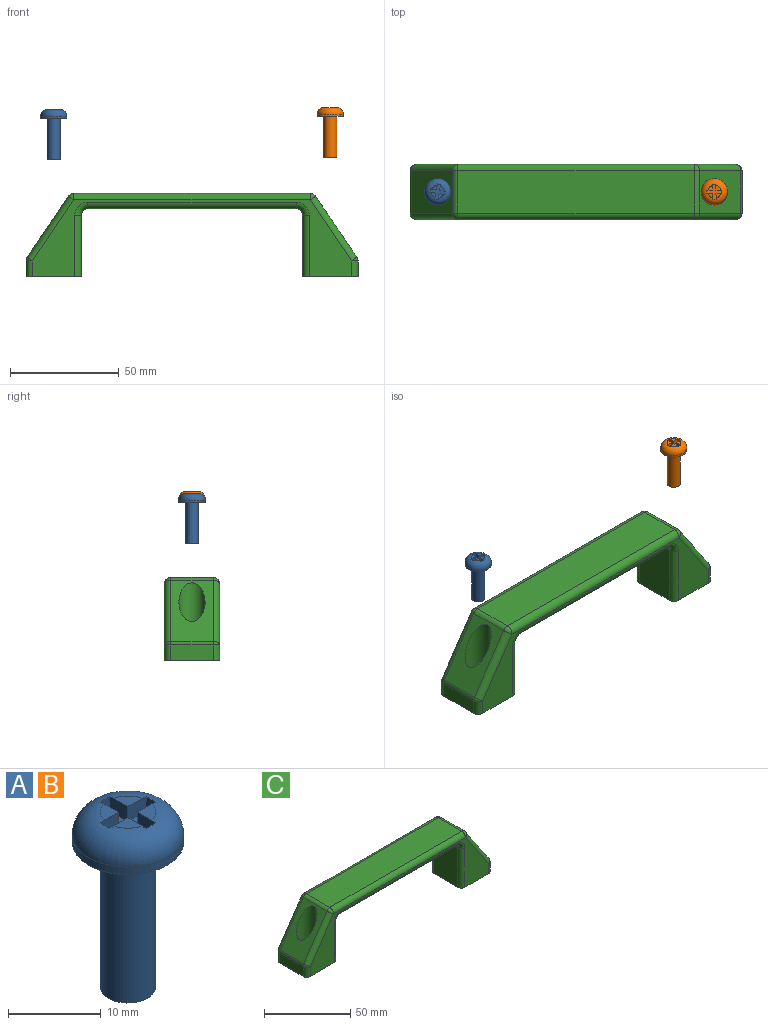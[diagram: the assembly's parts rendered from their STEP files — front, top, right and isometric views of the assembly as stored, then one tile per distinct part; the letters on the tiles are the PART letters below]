
ASSEMBLY  parts=3 mates=2
PART A: 22 faces, bbox 13x13x23.1 mm
  f0: plane 2.15x2.15mm, normal (0,0,1), area 3.2mm2, adj f3,f12,f13
  f1: plane 2.15x2.15mm, normal (0,0,1), area 3.2mm2, adj f3,f15,f16
  f2: plane 2.15x2.15mm, normal (0,0,1), area 3.2mm2, adj f3,f7,f18
  f3: torus R=3mm, axis (0,0,1), area 142.1mm2, adj f0,f1,f2,f4,f5,f7,f8,f9
  f4: cylinder r=6mm len=12mm, axis (0,0,-1), area 37.7mm2, adj f3,f6
  f5: plane 2.15x2.15mm, normal (0,0,1), area 3.2mm2, adj f3,f9,f10
  f6: plane 12x12mm, normal (0,0,-1), area 84.8mm2, adj f4,f20
  f7: plane 2.76x2.01mm, normal (-1,0,0), area 5.5mm2, adj f2,f3,f8,f18,f19
  f8: plane 1.96x1.5mm, normal (0,-1,0), area 2.9mm2, adj f3,f7,f9,f19
  f9: plane 2.76x2.01mm, normal (1,0,0), area 5.5mm2, adj f3,f5,f8,f10,f19
  f10: plane 2.76x2.01mm, normal (0,-1,0), area 5.5mm2, adj f3,f5,f9,f11,f19
  f11: plane 1.96x1.5mm, normal (1,0,0), area 2.9mm2, adj f3,f10,f12,f19
  f12: plane 2.76x2.01mm, normal (0,1,0), area 5.5mm2, adj f0,f3,f11,f13,f19
  f13: plane 2.76x2.01mm, normal (1,0,0), area 5.5mm2, adj f0,f3,f12,f14,f19
  f14: plane 1.96x1.5mm, normal (0,1,0), area 2.9mm2, adj f3,f13,f15,f19
  f15: plane 2.76x2.01mm, normal (-1,0,0), area 5.5mm2, adj f1,f3,f14,f16,f19
  f16: plane 2.76x2.01mm, normal (0,1,0), area 5.5mm2, adj f1,f3,f15,f17,f19
  f17: plane 2x1.54mm, normal (-1,0,0), area 2.9mm2, adj f3,f16,f18,f19
  f18: plane 2.76x2.01mm, normal (0,-1,0), area 5.5mm2, adj f2,f3,f7,f17,f19
  f19: plane 7x7mm, normal (0,0,1), area 18.8mm2, adj f7,f8,f9,f10,f11,f12,f13,f14
  f20: cylinder r=3mm len=19.05mm, axis (0,0,1), area 359.1mm2, adj f6,f21
  f21: plane 6x6mm, normal (0,0,-1), area 28.3mm2, adj f20
PART B: same geometry as A
PART C: 52 faces, bbox 156.1x29.1x41.8 mm
  f0: plane 28.1x19.4mm, normal (1,0,0), area 545.1mm2, adj f9,f20,f26,f29
  f1: plane 28.1x19.4mm, normal (-1,0,0), area 545.1mm2, adj f6,f18,f22,f23
  f2: plane 95.6x19.4mm, normal (0,0,-1), area 1854.6mm2, adj f21,f22,f26,f27
  f3: plane 19.4x7.08mm, normal (1,0,0), area 137.3mm2, adj f6,f36,f37,f38
  f4: plane 19.4x7.08mm, normal (-1,0,0), area 137.3mm2, adj f9,f30,f31,f32
  f5: plane 108.42x19.4mm, normal (0,0,1), area 2103.3mm2, adj f40,f45,f48,f51
  f6: plane 25.4x25.4mm, normal (0,0,-1), area 609.2mm2, adj f1,f3,f7,f8,f13,f18,f23,f36
  f7: plane 146.4x35.1mm, normal (0,1,0), area 952.8mm2, adj f6,f9,f23,f25,f27,f28,f29,f30
  f8: plane 146.4x35.1mm, normal (0,-1,0), area 952.8mm2, adj f6,f9,f18,f19,f20,f21,f24,f31
  f9: plane 25.4x25.4mm, normal (0,0,-1), area 609.2mm2, adj f0,f4,f7,f8,f12,f20,f29,f30
  f10: plane 28.02x19.4mm, normal (-0.83,0,0.56), area 455.1mm2, adj f16,f32,f35,f39,f40
  f11: plane 31.74x23.12mm, normal (0.83,0,0.56), area 455.1mm2, adj f15,f37,f46,f47,f51
  f12: cylinder r=3mm len=10mm, axis (0,0,-1), area 188.5mm2, adj f9,f17
  f13: cylinder r=3mm len=10mm, axis (0,0,-1), area 188.5mm2, adj f6,f14
  f14: plane 12x12mm, normal (0,0,1), area 84.8mm2, adj f13,f15
  f15: cylinder r=6mm len=25.59mm, axis (0,0,-1), area 631mm2, adj f11,f14
  f16: cylinder r=6mm len=25.71mm, axis (0,0,-1), area 631mm2, adj f10,f17
  f17: plane 12x12mm, normal (0,0,1), area 84.8mm2, adj f12,f16
  f18: cylinder r=3mm len=28.1mm, axis (0,0,-1), area 132.4mm2, adj f1,f6,f8,f19
  f19: torus R=6mm, axis (0,-1,0), area 30.3mm2, adj f8,f18,f21,f22
  f20: cylinder r=3mm len=28.1mm, axis (0,0,1), area 132.4mm2, adj f0,f8,f9,f24
  f21: cylinder r=3mm len=95.6mm, axis (1,0,0), area 450.5mm2, adj f2,f8,f19,f24
  f22: cylinder r=3mm len=19.4mm, axis (0,1,0), area 91.4mm2, adj f1,f2,f19,f25
  f23: cylinder r=3mm len=28.1mm, axis (0,0,1), area 132.4mm2, adj f1,f6,f7,f25
  f24: torus R=6mm, axis (0,-1,0), area 30.3mm2, adj f8,f20,f21,f26
  f25: torus R=6mm, axis (0,-1,0), area 30.3mm2, adj f7,f22,f23,f27
  f26: cylinder r=3mm len=19.4mm, axis (0,-1,0), area 91.4mm2, adj f0,f2,f24,f28
  f27: cylinder r=3mm len=95.6mm, axis (-1,0,0), area 450.5mm2, adj f2,f7,f25,f28
  f28: torus R=6mm, axis (0,-1,0), area 30.3mm2, adj f7,f26,f27,f29
  f29: cylinder r=3mm len=28.1mm, axis (0,0,-1), area 132.4mm2, adj f0,f7,f9,f28
  f30: cylinder r=3mm len=7.08mm, axis (0,0,-1), area 33.4mm2, adj f4,f7,f9,f33
  f31: cylinder r=3mm len=7.08mm, axis (0,0,1), area 33.4mm2, adj f4,f8,f9,f34
  f32: cylinder r=3mm len=19.4mm, axis (0,-1,0), area 34.7mm2, adj f4,f10,f33,f34
  f33: sphere r=3mm, area 5.4mm2, adj f30,f32,f35
  f34: sphere r=3mm, area 5.2mm2, adj f31,f32,f39
  f35: cylinder r=3mm len=29.7mm, axis (0.56,0,0.83), area 159.5mm2, adj f7,f10,f33,f41
  f36: cylinder r=3mm len=7.08mm, axis (0,0,1), area 33.4mm2, adj f3,f6,f7,f42
  f37: cylinder r=3mm len=19.4mm, axis (0,-1,0), area 34.7mm2, adj f3,f11,f42,f43
  f38: cylinder r=3mm len=7.08mm, axis (0,0,-1), area 33.4mm2, adj f3,f6,f8,f43
  f39: cylinder r=3mm len=29.7mm, axis (-0.56,0,-0.83), area 159.5mm2, adj f8,f10,f34,f44
  f40: cylinder r=3mm len=19.4mm, axis (0,1,0), area 56.8mm2, adj f5,f10,f41,f44
  f41: sphere r=3mm, area 8.8mm2, adj f35,f40,f45
  f42: sphere r=3mm, area 5.4mm2, adj f36,f37,f46
  f43: sphere r=3mm, area 5.4mm2, adj f37,f38,f47
  f44: sphere r=3mm, area 8.8mm2, adj f39,f40,f48
  f45: cylinder r=3mm len=108.42mm, axis (1,0,0), area 510.9mm2, adj f5,f7,f41,f49
  f46: cylinder r=3mm len=29.7mm, axis (0.56,0,-0.83), area 159.5mm2, adj f7,f11,f42,f49
  f47: cylinder r=3mm len=29.7mm, axis (-0.56,0,0.83), area 159.5mm2, adj f8,f11,f43,f50
  f48: cylinder r=3mm len=108.42mm, axis (-1,0,0), area 510.9mm2, adj f5,f8,f44,f50
  f49: sphere r=3mm, area 5.6mm2, adj f45,f46,f51
  f50: sphere r=3mm, area 8.8mm2, adj f47,f48,f51
  f51: cylinder r=3mm len=19.4mm, axis (0,-1,0), area 56.8mm2, adj f5,f11,f49,f50
PLACE A rot(axis=(0,0,1),169.7deg) t=(-164.95,4.17,62.47)mm
PLACE B rot(axis=(0,0,1),0.6deg) t=(88.03,-6.52,63.42)mm
PLACE C t=(-38.97,-7.19,-0.08)mm fixed
MATE cylindrical B.f3 <-> C.f13  axis (0,0,-1) through (24.53,-7.19,73.42)mm
MATE cylindrical A.f3 <-> C.f16  axis (0,0,-1) through (-102.47,-7.19,72.47)mm
